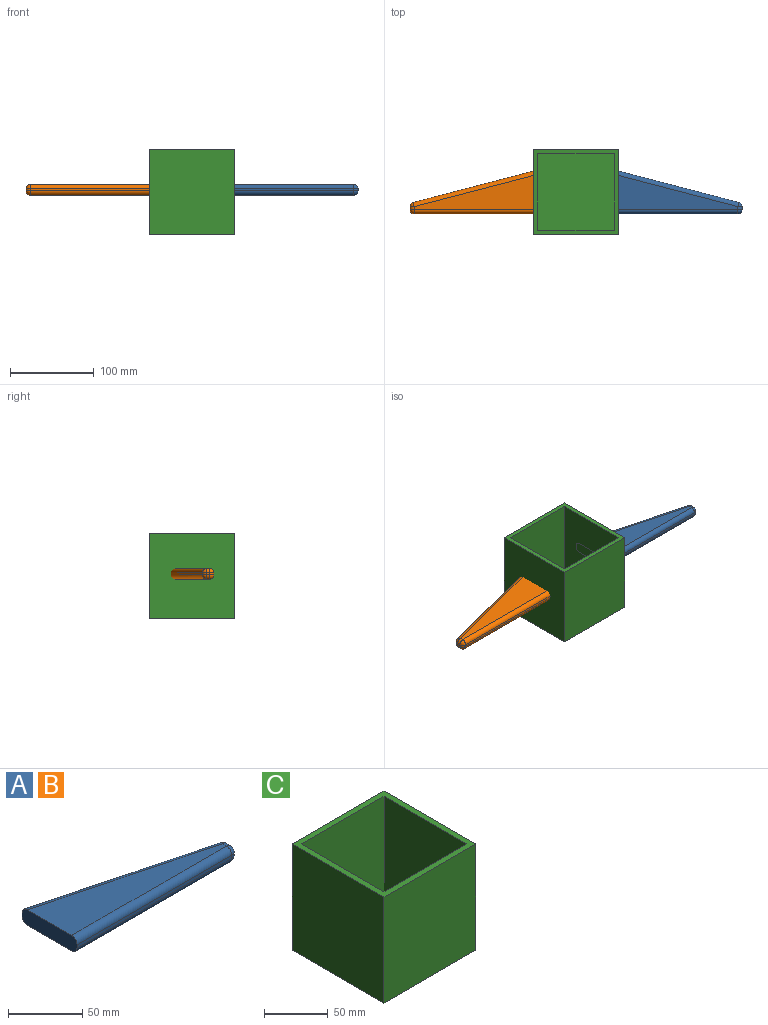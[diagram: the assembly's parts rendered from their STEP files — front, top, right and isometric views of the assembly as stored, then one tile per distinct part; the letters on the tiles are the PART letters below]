
ASSEMBLY  parts=3 mates=2
PART A: 18 faces, bbox 153.7x52.4x12.7 mm
  f0: plane 148.6x38.69mm, normal (0.25,0.97,0), area 390mm2, adj f1,f6,f7,f8
  f1: plane 52.38x12.7mm, normal (-1,0,0), area 642.7mm2, adj f0,f2,f4,f5,f6,f8,f11,f14
  f2: plane 147.32x2.54mm, normal (0,-1,0), area 374.2mm2, adj f1,f11,f14,f17
  f3: plane 3.69x2.54mm, normal (1,0,0), area 9.4mm2, adj f7,f12,f13,f17
  f4: plane 147.32x42.05mm, normal (0,0,1), area 3369.2mm2, adj f1,f6,f11,f12
  f5: plane 147.32x42.05mm, normal (0,0,-1), area 3369.2mm2, adj f1,f8,f13,f14
  f6: cylinder r=5.08mm len=149.88mm, axis (0.97,-0.25,0), area 1221.5mm2, adj f0,f1,f4,f9
  f7: cylinder r=5.08mm len=4.92mm, axis (0,0,-1), area 17mm2, adj f0,f3,f9,f10
  f8: cylinder r=5.08mm len=149.88mm, axis (-0.97,0.25,0), area 1221.5mm2, adj f0,f1,f5,f10
  f9: sphere r=5.08mm, area 34mm2, adj f6,f7,f12
  f10: sphere r=5.08mm, area 34mm2, adj f7,f8,f13
  f11: cylinder r=5.08mm len=147.32mm, axis (-1,0,0), area 1175.6mm2, adj f1,f2,f4,f15
  f12: cylinder r=5.08mm len=5.08mm, axis (0,-1,0), area 29.5mm2, adj f3,f4,f9,f15
  f13: cylinder r=5.08mm len=5.08mm, axis (0,1,0), area 29.5mm2, adj f3,f5,f10,f16
  f14: cylinder r=5.08mm len=147.32mm, axis (1,0,0), area 1175.6mm2, adj f1,f2,f5,f16
  f15: sphere r=5.08mm, area 40.5mm2, adj f11,f12,f17
  f16: sphere r=5.08mm, area 40.5mm2, adj f13,f14,f17
  f17: cylinder r=5.08mm len=5.08mm, axis (0,0,-1), area 20.3mm2, adj f2,f3,f15,f16
PART B: same geometry as A
PART C: 11 faces, bbox 101.6x101.6x101.6 mm
  f0: plane 101.6x101.6mm, normal (0,0,1), area 1961.3mm2, adj f1,f2,f3,f4,f6,f7,f8,f9
  f1: plane 101.6x101.6mm, normal (0,-1,0), area 10322.6mm2, adj f0,f2,f4,f5
  f2: plane 101.6x101.6mm, normal (1,0,0), area 10322.6mm2, adj f0,f1,f3,f5
  f3: plane 101.6x101.6mm, normal (0,1,0), area 10322.6mm2, adj f0,f2,f4,f5
  f4: plane 101.6x101.6mm, normal (-1,0,0), area 10322.6mm2, adj f0,f1,f3,f5
  f5: plane 101.6x101.6mm, normal (0,0,-1), area 10322.6mm2, adj f1,f2,f3,f4
  f6: plane 96.52x91.44mm, normal (0,1,0), area 8825.8mm2, adj f0,f7,f9,f10
  f7: plane 96.52x91.44mm, normal (-1,0,0), area 8825.8mm2, adj f0,f6,f8,f10
  f8: plane 96.52x91.44mm, normal (0,-1,0), area 8825.8mm2, adj f0,f7,f9,f10
  f9: plane 96.52x91.44mm, normal (1,0,0), area 8825.8mm2, adj f0,f6,f8,f10
  f10: plane 91.44x91.44mm, normal (0,0,1), area 8361.3mm2, adj f6,f7,f8,f9
PLACE A t=(45.72,-13.47,46.99)mm
PLACE B rot(axis=(0,1,0),180deg) t=(-45.72,-13.47,59.69)mm
PLACE C at identity
MATE planar B.f1 <-> C.f9  axis (1,0,0) through (-45.72,0,53.34)mm
MATE planar A.f1 <-> C.f7  axis (-1,0,0) through (45.72,0,53.34)mm
